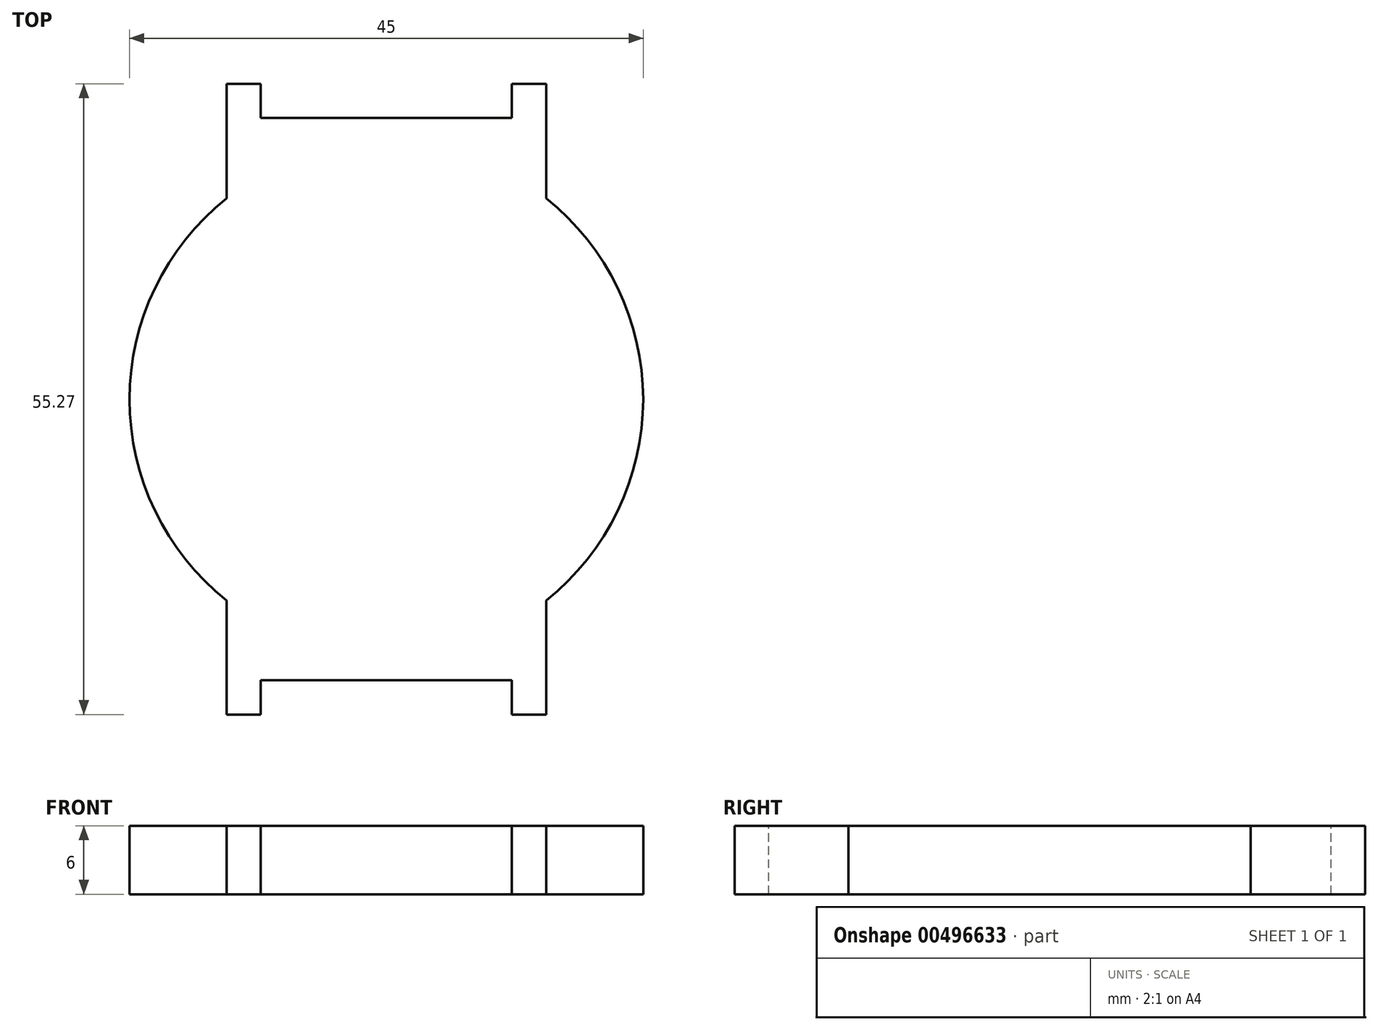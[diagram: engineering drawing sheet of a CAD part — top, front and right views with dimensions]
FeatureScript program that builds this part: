
annotation { "Feature Type Name" : "Feature", "Feature Type Description" : "" }
export const myFeature = defineFeature(function(context is Context, id is Id, definition is map)
    precondition{}
    {
        {
            var Q0;
            Q0=qCreatedBy(makeId("Top.planeOp"),FACE);
            var sketch = newSketch(context, id + "F0", { "sketchPlane" : qUnion([Q0])});
            skLineSegment(sketch, "E0", {"start": v(0, 0) * mm, "end": v(-28, 0) * mm});
            skLineSegment(sketch, "E1", {"start": v(-28, 0) * mm, "end": v(-28, 10) * mm});
            skLineSegment(sketch, "E2", {"start": v(0, 0) * mm, "end": v(0, 10) * mm});
            skArc(sketch, "E3", {"start": v(0, 10) * mm, "mid": v(8.5, 27.61) * mm, "end": v(0, 45.23) * mm});
            skPoint(sketch, "E3.third.point", {"position": v(-5, 48.24) * mm});
            skLineSegment(sketch, "E4", {"start": v(-28, 55.27) * mm, "end": v(0, 55.27) * mm});
            skLineSegment(sketch, "E5", {"start": v(-28, 55.27) * mm, "end": v(-28, 45.23) * mm});
            skLineSegment(sketch, "E6", {"start": v(0, 55.27) * mm, "end": v(0, 45.23) * mm});
            skArc(sketch, "E7.trimOffspring", {"start": v(-28, 45.23) * mm, "mid": v(-36.5, 27.61) * mm, "end": v(-28, 10) * mm});
            skSolve(sketch);
        }
        {
            var Q0;
            Q0=makeQuery(id+"F0.imprint","IMPRINT",FACE,{"disambiguationData":[TD([[makeQuery(id+"F0.imprint","IMPRINT",EDGE,{"derivedFrom":sQuery(id+"F0.wireOp",EDGE,"E0")}),-1.0]])]});
            extrude(context, id + "F1", {"entities" : qUnion([Q0]), "depth" : 6 * mm, "offsetDistance" : 25 * mm});
        }
        {
            var Q0;
            Q0=makeQuery(id+"F1.opExtrude","CAP_FACE",FACE,{"disambiguationData":[OSD([sQuery(id+"F0.wireOp",EDGE,"E0"),sQuery(id+"F0.wireOp",EDGE,"E1"),sQuery(id+"F0.wireOp",EDGE,"E2"),sQuery(id+"F0.wireOp",EDGE,"E3"),sQuery(id+"F0.wireOp",EDGE,"E4"),sQuery(id+"F0.wireOp",EDGE,"E5"),sQuery(id+"F0.wireOp",EDGE,"E6"),sQuery(id+"F0.wireOp",EDGE,"E7.trimOffspring")])],"isStart":false});
            var sketch = newSketch(context, id + "F2", { "sketchPlane" : qUnion([Q0])});
            skLineSegment(sketch, "E8.bottom", {"start": v(-25, 55.27) * mm, "end": v(-3, 55.27) * mm});
            skLineSegment(sketch, "E8.top", {"start": v(-25, 52.27) * mm, "end": v(-3, 52.27) * mm});
            skLineSegment(sketch, "E8.left", {"start": v(-25, 55.27) * mm, "end": v(-25, 52.27) * mm});
            skLineSegment(sketch, "E8.right", {"start": v(-3, 55.27) * mm, "end": v(-3, 52.27) * mm});
            skLineSegment(sketch, "E9.bottom", {"start": v(-25, 0) * mm, "end": v(-3, 0) * mm});
            skLineSegment(sketch, "E9.top", {"start": v(-25, 3) * mm, "end": v(-3, 3) * mm});
            skLineSegment(sketch, "E9.left", {"start": v(-25, 0) * mm, "end": v(-25, 3) * mm});
            skLineSegment(sketch, "E9.right", {"start": v(-3, 0) * mm, "end": v(-3, 3) * mm});
            skSolve(sketch);
        }
        {
            var Q0;
            Q0 = qSketchRegion(id + "F2", true);
            extrude(context, id + "F3", {"entities" : qUnion([Q0]), "operationType" : NewBodyOperationType.REMOVE, "endBound" : BoundingType.UP_TO_NEXT, "oppositeDirection" : true, "depth" : 25 * mm, "offsetDistance" : 25 * mm});
        }
    });
